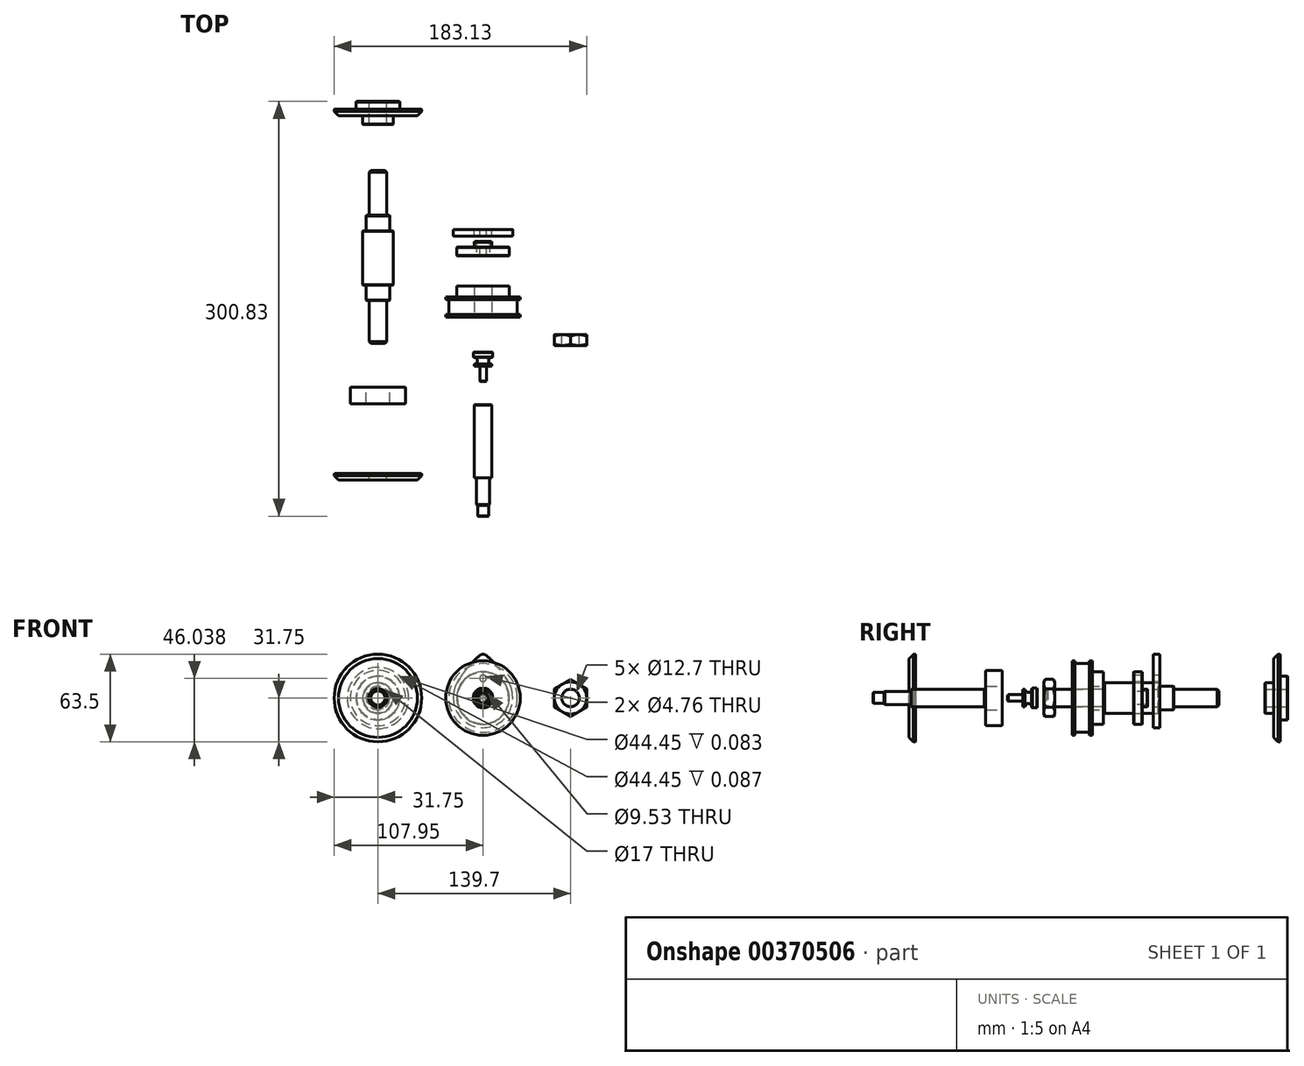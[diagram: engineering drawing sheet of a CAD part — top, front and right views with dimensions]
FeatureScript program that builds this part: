
annotation { "Feature Type Name" : "Feature", "Feature Type Description" : "" }
export const myFeature = defineFeature(function(context is Context, id is Id, definition is map)
    precondition{}
    {
        {
            var Q0;
            Q0=qCreatedBy(makeId("Right.planeOp"),FACE);
            var sketch = newSketch(context, id + "F0", { "sketchPlane" : qUnion([Q0])});
            skLineSegment(sketch, "E0", {"start": v(-34.13, 0) * mm, "end": v(-34.13, 2.38) * mm});
            skLineSegment(sketch, "E1", {"start": v(-34.13, 2.38) * mm, "end": v(-23.02, 2.38) * mm});
            skLineSegment(sketch, "E2", {"start": v(-23.02, 2.38) * mm, "end": v(-23.02, 6.35) * mm});
            skLineSegment(sketch, "E3", {"start": v(-23.02, 6.35) * mm, "end": v(-21.43, 6.35) * mm});
            skLineSegment(sketch, "E4", {"start": v(-16.67, 6.35) * mm, "end": v(-16.67, 7.14) * mm});
            skLineSegment(sketch, "E5", {"start": v(-16.67, 7.14) * mm, "end": v(-12.7, 7.14) * mm});
            skLineSegment(sketch, "E6", {"start": v(-12.7, 7.14) * mm, "end": v(-12.7, 0) * mm});
            skLineSegment(sketch, "E7", {"start": v(0, 0) * mm, "end": v(-162.62, 0) * mm, "construction": true});
            skLineSegment(sketch, "E8", {"start": v(-12.7, 0) * mm, "end": v(-34.13, 0) * mm});
            skArc(sketch, "E9", {"start": v(-21.43, 6.35) * mm, "mid": v(-19.05, 3.97) * mm, "end": v(-16.67, 6.35) * mm});
            skSolve(sketch);
        }
        {
            var Q0;
            Q0=makeQuery(id+"F0.imprint","IMPRINT",FACE,{"disambiguationData":[TD([[makeQuery(id+"F0.imprint","IMPRINT",EDGE,{"derivedFrom":sQuery(id+"F0.wireOp",EDGE,"E0")}),-1.0]])]});
            var Q1;
            Q1=sQuery(id+"F0.wireOp",EDGE,"E7");
            revolve(context, id + "F1", {"entities" : qUnion([Q0]), "axis" : qUnion([Q1]), "revolveType" : RevolveType.FULL});
        }
        {
            var Q0;
            Q0=makeQuery(id+"F1.opRevolve","SWEPT_FACE",FACE,{"disambiguationData":[OSD([sQuery(id+"F0.wireOp",EDGE,"E5")])]});
            var Q1;
            Q1=makeQuery(id+"F1.opRevolve","SWEPT_EDGE",EDGE,{"disambiguationData":[OSD([sQuery(id+"F0.wireOp",EDGE,"E0"),sQuery(id+"F0.wireOp",EDGE,"E1")])]});
            chamfer(context, id + "F2", {"entities" : qUnion([Q0, Q1]), "width" : 0.4 * mm, "tangentPropagation" : true});
        }
        {
            var Q0;
            Q0=makeQuery(id+"F1.opRevolve","SWEPT_EDGE",EDGE,{"disambiguationData":[OSD([sQuery(id+"F0.wireOp",EDGE,"E1"),sQuery(id+"F0.wireOp",EDGE,"E2")])]});
            fillet(context, id + "F3", {"entities" : qUnion([Q0]), "radius" : 0.4 * mm, "tangentPropagation" : true, "allowEdgeOverflow" : false});
        }
        {
            var Q0;
            Q0=qCreatedBy(makeId("Right.planeOp"),FACE);
            var sketch = newSketch(context, id + "F4", { "sketchPlane" : qUnion([Q0])});
            skLineSegment(sketch, "E10", {"start": v(0, 0) * mm, "end": v(30.35, 0) * mm, "construction": true});
            skLineSegment(sketch, "E11", {"start": v(12.7, 6.35) * mm, "end": v(12.7, 27) * mm});
            skLineSegment(sketch, "E12", {"start": v(12.7, 27) * mm, "end": v(14.7, 27) * mm});
            skLineSegment(sketch, "E13", {"start": v(14.7, 27) * mm, "end": v(14.7, 24.9) * mm});
            skLineSegment(sketch, "E14", {"start": v(14.7, 24.9) * mm, "end": v(25.2, 24.9) * mm});
            skLineSegment(sketch, "E15", {"start": v(25.2, 24.9) * mm, "end": v(25.2, 27) * mm});
            skLineSegment(sketch, "E16", {"start": v(25.2, 27) * mm, "end": v(27.2, 27) * mm});
            skLineSegment(sketch, "E17", {"start": v(27.2, 27) * mm, "end": v(27.2, 19) * mm});
            skLineSegment(sketch, "E18", {"start": v(27.2, 19) * mm, "end": v(35.2, 19) * mm});
            skLineSegment(sketch, "E19", {"start": v(35.2, 19) * mm, "end": v(35.2, 6.35) * mm});
            skLineSegment(sketch, "E20", {"start": v(35.2, 6.35) * mm, "end": v(12.7, 6.35) * mm});
            skSolve(sketch);
        }
        {
            var Q0;
            Q0=makeQuery(id+"F4.imprint","IMPRINT",FACE,{"disambiguationData":[TD([[makeQuery(id+"F4.imprint","IMPRINT",EDGE,{"derivedFrom":sQuery(id+"F4.wireOp",EDGE,"E11")}),-1.0]])]});
            var Q1;
            Q1=sQuery(id+"F4.wireOp",EDGE,"E10");
            revolve(context, id + "F5", {"entities" : qUnion([Q0]), "axis" : qUnion([Q1]), "revolveType" : RevolveType.FULL});
        }
        {
            var Q0;
            Q0=qCreatedBy(makeId("Right.planeOp"),FACE);
            var sketch = newSketch(context, id + "F6", { "sketchPlane" : qUnion([Q0])});
            skLineSegment(sketch, "E21", {"start": v(0, 0) * mm, "end": v(-138.04, 0) * mm, "construction": true});
            skLineSegment(sketch, "E22", {"start": v(-131.76, 0) * mm, "end": v(-131.76, 3.97) * mm});
            skLineSegment(sketch, "E23", {"start": v(-131.76, 3.97) * mm, "end": v(-123.83, 3.97) * mm});
            skLineSegment(sketch, "E24", {"start": v(-123.83, 3.97) * mm, "end": v(-123.83, 4.76) * mm});
            skLineSegment(sketch, "E25", {"start": v(-123.83, 4.76) * mm, "end": v(-103.98, 4.76) * mm});
            skLineSegment(sketch, "E26", {"start": v(-103.98, 4.76) * mm, "end": v(-103.98, 6.35) * mm});
            skLineSegment(sketch, "E27", {"start": v(-103.98, 6.35) * mm, "end": v(-50.8, 6.35) * mm});
            skLineSegment(sketch, "E28", {"start": v(-50.8, 6.35) * mm, "end": v(-50.8, 0) * mm});
            skLineSegment(sketch, "E29", {"start": v(-50.8, 0) * mm, "end": v(-131.76, 0) * mm});
            skSolve(sketch);
        }
        {
            var Q0;
            Q0=makeQuery(id+"F6.imprint","IMPRINT",FACE,{"disambiguationData":[TD([[makeQuery(id+"F6.imprint","IMPRINT",EDGE,{"derivedFrom":sQuery(id+"F6.wireOp",EDGE,"E22")}),-1.0]])]});
            var Q1;
            Q1=sQuery(id+"F6.wireOp",EDGE,"E21");
            revolve(context, id + "F7", {"entities" : qUnion([Q0]), "axis" : qUnion([Q1]), "revolveType" : RevolveType.FULL});
        }
        {
            var Q0;
            Q0=makeQuery(id+"F7.opRevolve","SWEPT_EDGE",EDGE,{"disambiguationData":[OSD([sQuery(id+"F6.wireOp",EDGE,"E27"),sQuery(id+"F6.wireOp",EDGE,"E28")])]});
            var Q1;
            Q1=makeQuery(id+"F7.opRevolve","SWEPT_EDGE",EDGE,{"disambiguationData":[OSD([sQuery(id+"F6.wireOp",EDGE,"E22"),sQuery(id+"F6.wireOp",EDGE,"E23")])]});
            chamfer(context, id + "F8", {"entities" : qUnion([Q0, Q1]), "width" : 0.4 * mm, "tangentPropagation" : true});
        }
        {
            var Q0;
            Q0=makeQuery(id+"F7.opRevolve","SWEPT_EDGE",EDGE,{"disambiguationData":[OSD([sQuery(id+"F6.wireOp",EDGE,"E24"),sQuery(id+"F6.wireOp",EDGE,"E25")])]});
            chamfer(context, id + "F9", {"entities" : qUnion([Q0]), "width" : 0.64 * mm, "tangentPropagation" : true});
        }
        {
            var Q0;
            Q0=makeQuery(id+"F7.opRevolve","SWEPT_EDGE",EDGE,{"disambiguationData":[OSD([sQuery(id+"F6.wireOp",EDGE,"E25"),sQuery(id+"F6.wireOp",EDGE,"E26")])]});
            fillet(context, id + "F10", {"entities" : qUnion([Q0]), "radius" : 0.4 * mm, "tangentPropagation" : true, "allowEdgeOverflow" : false});
        }
        {
            var Q0;
            Q0=qCreatedBy(makeId("Right.planeOp"),FACE);
            var sketch = newSketch(context, id + "F11", { "sketchPlane" : qUnion([Q0])});
            skLineSegment(sketch, "E30", {"start": v(0, 0) * mm, "end": v(68.22, 0) * mm, "construction": true});
            skLineSegment(sketch, "E31", {"start": v(67.47, 4.76) * mm, "end": v(57.15, 4.76) * mm});
            skLineSegment(sketch, "E32", {"start": v(57.15, 4.76) * mm, "end": v(57.15, 19.05) * mm});
            skLineSegment(sketch, "E33", {"start": v(57.15, 19.05) * mm, "end": v(63.5, 19.05) * mm});
            skLineSegment(sketch, "E34", {"start": v(63.5, 19.05) * mm, "end": v(63.5, 6.35) * mm});
            skLineSegment(sketch, "E35", {"start": v(63.5, 6.35) * mm, "end": v(67.47, 6.35) * mm});
            skLineSegment(sketch, "E36", {"start": v(67.47, 6.35) * mm, "end": v(67.47, 4.76) * mm});
            skSolve(sketch);
        }
        {
            var Q0;
            Q0=makeQuery(id+"F11.imprint","IMPRINT",FACE,{"disambiguationData":[TD([[makeQuery(id+"F11.imprint","IMPRINT",EDGE,{"derivedFrom":sQuery(id+"F11.wireOp",EDGE,"E31")}),-1.0]])]});
            var Q1;
            Q1=sQuery(id+"F11.wireOp",EDGE,"E30");
            revolve(context, id + "F12", {"entities" : qUnion([Q0]), "axis" : qUnion([Q1]), "revolveType" : RevolveType.FULL});
        }
        {
            var Q0;
            Q0=makeQuery(id+"F12.opRevolve","SWEPT_FACE",FACE,{"disambiguationData":[OSD([sQuery(id+"F11.wireOp",EDGE,"E36")])]});
            var Q1;
            Q1=makeQuery(id+"F12.opRevolve","SWEPT_FACE",FACE,{"disambiguationData":[OSD([sQuery(id+"F11.wireOp",EDGE,"E33")])]});
            var Q2;
            Q2=makeQuery(id+"F12.opRevolve","SWEPT_EDGE",EDGE,{"disambiguationData":[OSD([sQuery(id+"F11.wireOp",EDGE,"E31"),sQuery(id+"F11.wireOp",EDGE,"E32")])]});
            chamfer(context, id + "F13", {"entities" : qUnion([Q0, Q1, Q2]), "width" : 0.4 * mm, "tangentPropagation" : true});
        }
        {
            var Q0;
            Q0=makeQuery(id+"F12.opRevolve","SWEPT_EDGE",EDGE,{"disambiguationData":[OSD([sQuery(id+"F11.wireOp",EDGE,"E34"),sQuery(id+"F11.wireOp",EDGE,"E35")])]});
            fillet(context, id + "F14", {"entities" : qUnion([Q0]), "radius" : 0.4 * mm, "tangentPropagation" : true, "allowEdgeOverflow" : false});
        }
        {
            var Q0;
            Q0=qCreatedBy(makeId("Front.planeOp"),FACE);
            cPlane(context, id + "F15", {"entities" : qUnion([Q0]), "cplaneType" : CPlaneType.OFFSET, "offset" : 76.2 * mm, "oppositeDirection" : true, "width" : 152.4 * mm, "height" : 152.4 * mm});
        }
        {
            var Q0;
            Q0=qCreatedBy(id+"F15.planeOp",FACE);
            var sketch = newSketch(context, id + "F16", { "sketchPlane" : qUnion([Q0])});
            skCircle(sketch, "E37", {"center": v(0, 0) * mm, "radius": 6.35 * mm});
            skArc(sketch, "E38", {"start": v(-21.38, 2.39) * mm, "mid": v(-0.06, -21.51) * mm, "end": v(21.4, 2.27) * mm});
            skCircle(sketch, "E39", {"center": v(0, 14.29) * mm, "radius": 2.38 * mm});
            skArc(sketch, "E40", {"start": v(2.18, 30.95) * mm, "mid": v(0, 31.74) * mm, "end": v(-2.18, 30.95) * mm});
            skLineSegment(sketch, "E41", {"start": v(0, 0) * mm, "end": v(-43.39, -24.05) * mm, "construction": true});
            skLineSegment(sketch, "E42", {"start": v(0, 0) * mm, "end": v(43.39, -24.05) * mm, "construction": true});
            skArc(sketch, "E43", {"start": v(-2.18, 30.95) * mm, "mid": v(-11.58, 21.55) * mm, "end": v(-19.08, 10.58) * mm});
            skArc(sketch, "E44.trimOffspring", {"start": v(19.1, 10.58) * mm, "mid": v(11.59, 21.56) * mm, "end": v(2.18, 30.95) * mm});
            skLineSegment(sketch, "E45", {"start": v(0, 0) * mm, "end": v(19.1, 10.58) * mm, "construction": true});
            skArc(sketch, "E46", {"start": v(21.23, 3.8) * mm, "mid": v(20.5, 7.3) * mm, "end": v(19.1, 10.58) * mm});
            skLineSegment(sketch, "E47", {"start": v(21.4, 2.27) * mm, "end": v(21.23, 3.8) * mm});
            skLineSegment(sketch, "E48", {"start": v(0, 0) * mm, "end": v(-19.08, 10.58) * mm, "construction": true});
            skArc(sketch, "E49", {"start": v(-19.08, 10.58) * mm, "mid": v(-20.48, 7.35) * mm, "end": v(-21.21, 3.9) * mm});
            skLineSegment(sketch, "E50", {"start": v(-21.21, 3.9) * mm, "end": v(-21.38, 2.39) * mm});
            skSolve(sketch);
        }
        {
            var Q0;
            Q0=makeQuery(id+"F16.imprint","IMPRINT",FACE,{"disambiguationData":[TD([[makeQuery(id+"F16.imprint","IMPRINT",EDGE,{"derivedFrom":sQuery(id+"F16.wireOp",EDGE,"E37")}),-1.0]])]});
            extrude(context, id + "F17", {"entities" : qUnion([Q0]), "depth" : 4.76 * mm});
        }
        {
            var Q0;
            Q0=makeQuery(id+"F16.imprint","IMPRINT",FACE,{"disambiguationData":[TD([[makeQuery(id+"F16.imprint","IMPRINT",EDGE,{"derivedFrom":sQuery(id+"F16.wireOp",EDGE,"E39")}),1.0]])]});
            extrude(context, id + "F18", {"entities" : qUnion([Q0]), "operationType" : NewBodyOperationType.REMOVE, "depth" : 25.4 * mm});
        }
        {
            var Q0;
            Q0=qCreatedBy(makeId("Top.planeOp"),FACE);
            var sketch = newSketch(context, id + "F19", { "sketchPlane" : qUnion([Q0])});
            skLineSegment(sketch, "E51", {"start": v(-76.2, 204.41) * mm, "end": v(-76.2, -130.74) * mm, "construction": true});
            skLineSegment(sketch, "E52", {"start": v(-98.42, -100.8) * mm, "end": v(-107.95, -100.8) * mm});
            skLineSegment(sketch, "E53", {"start": v(-107.95, -100.8) * mm, "end": v(-107.95, -102.39) * mm});
            skLineSegment(sketch, "E54", {"start": v(-107.95, -102.39) * mm, "end": v(-104.77, -105.56) * mm});
            skLineSegment(sketch, "E55", {"start": v(-104.77, -105.56) * mm, "end": v(-82.55, -105.56) * mm});
            skLineSegment(sketch, "E56", {"start": v(-82.55, -105.56) * mm, "end": v(-82.55, -101.6) * mm});
            skLineSegment(sketch, "E57", {"start": v(-82.55, -101.6) * mm, "end": v(-98.42, -101.6) * mm});
            skLineSegment(sketch, "E58", {"start": v(-98.42, -101.6) * mm, "end": v(-98.42, -100.8) * mm});
            skLineSegment(sketch, "E59.bottom", {"start": v(-95.6, -50.1) * mm, "end": v(-85.3, -50.1) * mm});
            skLineSegment(sketch, "E59.top", {"start": v(-95.6, -38.1) * mm, "end": v(-85.3, -38.1) * mm});
            skLineSegment(sketch, "E59.left", {"start": v(-96.2, -49.5) * mm, "end": v(-96.2, -38.7) * mm});
            skLineSegment(sketch, "E59.right", {"start": v(-84.7, -49.5) * mm, "end": v(-84.7, -38.7) * mm});
            skPoint(sketch, "E60.visualSharp", {"position": v(-96.2, -50.1) * mm});
            skArc(sketch, "E60.filletArc", {"start": v(-96.2, -49.5) * mm, "mid": v(-96.02, -49.92) * mm, "end": v(-95.6, -50.1) * mm});
            skPoint(sketch, "E61.visualSharp", {"position": v(-96.2, -38.1) * mm});
            skArc(sketch, "E61.filletArc", {"start": v(-95.6, -38.1) * mm, "mid": v(-96.02, -38.28) * mm, "end": v(-96.2, -38.7) * mm});
            skPoint(sketch, "E62.visualSharp", {"position": v(-84.7, -38.1) * mm});
            skArc(sketch, "E62.filletArc", {"start": v(-84.7, -38.7) * mm, "mid": v(-84.88, -38.28) * mm, "end": v(-85.3, -38.1) * mm});
            skPoint(sketch, "E63.visualSharp", {"position": v(-84.7, -50.1) * mm});
            skArc(sketch, "E63.filletArc", {"start": v(-85.3, -50.1) * mm, "mid": v(-84.88, -49.92) * mm, "end": v(-84.7, -49.5) * mm});
            skLineSegment(sketch, "E64", {"start": v(-76.2, -6.35) * mm, "end": v(-82.55, -6.35) * mm});
            skLineSegment(sketch, "E65", {"start": v(-82.55, -6.35) * mm, "end": v(-82.55, 24.6) * mm});
            skLineSegment(sketch, "E66", {"start": v(-82.55, 24.6) * mm, "end": v(-84.7, 24.6) * mm});
            skLineSegment(sketch, "E67", {"start": v(-84.7, 24.6) * mm, "end": v(-84.7, 35.81) * mm});
            skLineSegment(sketch, "E68", {"start": v(-84.7, 35.81) * mm, "end": v(-87.31, 35.81) * mm});
            skLineSegment(sketch, "E69", {"start": v(-87.31, 35.81) * mm, "end": v(-87.31, 75.31) * mm});
            skLineSegment(sketch, "E70", {"start": v(-87.31, 75.31) * mm, "end": v(-84.7, 75.31) * mm});
            skLineSegment(sketch, "E71", {"start": v(-84.7, 75.31) * mm, "end": v(-84.7, 86.5) * mm});
            skLineSegment(sketch, "E72", {"start": v(-84.7, 86.5) * mm, "end": v(-82.55, 86.5) * mm});
            skLineSegment(sketch, "E73", {"start": v(-82.55, 86.5) * mm, "end": v(-82.55, 119.05) * mm});
            skLineSegment(sketch, "E74", {"start": v(-82.55, 119.05) * mm, "end": v(-76.2, 119.05) * mm});
            skLineSegment(sketch, "E75", {"start": v(-76.2, 119.05) * mm, "end": v(-76.2, -6.35) * mm});
            skLineSegment(sketch, "E76", {"start": v(-82.55, 152.4) * mm, "end": v(-87.31, 152.4) * mm});
            skLineSegment(sketch, "E77", {"start": v(-87.31, 152.4) * mm, "end": v(-87.31, 158.75) * mm});
            skLineSegment(sketch, "E78", {"start": v(-87.31, 158.75) * mm, "end": v(-104.78, 158.75) * mm});
            skLineSegment(sketch, "E79", {"start": v(-104.78, 158.75) * mm, "end": v(-107.95, 161.93) * mm});
            skLineSegment(sketch, "E80", {"start": v(-107.95, 161.93) * mm, "end": v(-107.95, 163.51) * mm});
            skLineSegment(sketch, "E81", {"start": v(-107.95, 163.51) * mm, "end": v(-98.43, 163.51) * mm});
            skLineSegment(sketch, "E82", {"start": v(-98.43, 163.51) * mm, "end": v(-98.43, 162.72) * mm});
            skLineSegment(sketch, "E83", {"start": v(-98.43, 162.72) * mm, "end": v(-92.08, 162.72) * mm});
            skLineSegment(sketch, "E84", {"start": v(-92.08, 162.72) * mm, "end": v(-92.08, 169.07) * mm});
            skLineSegment(sketch, "E85", {"start": v(-92.08, 169.07) * mm, "end": v(-82.55, 169.07) * mm});
            skLineSegment(sketch, "E86", {"start": v(-82.55, 169.07) * mm, "end": v(-82.55, 152.4) * mm});
            skSolve(sketch);
        }
        {
            var Q0;
            Q0=makeQuery(id+"F19.imprint","IMPRINT",FACE,{"disambiguationData":[TD([[makeQuery(id+"F19.imprint","IMPRINT",EDGE,{"derivedFrom":sQuery(id+"F19.wireOp",EDGE,"E52")}),1.0]])]});
            var Q1;
            Q1=makeQuery(id+"F19.imprint","IMPRINT",FACE,{"disambiguationData":[TD([[makeQuery(id+"F19.imprint","IMPRINT",EDGE,{"derivedFrom":sQuery(id+"F19.wireOp",EDGE,"E59.bottom")}),1.0]])]});
            var Q2;
            Q2=makeQuery(id+"F19.imprint","IMPRINT",FACE,{"disambiguationData":[TD([[makeQuery(id+"F19.imprint","IMPRINT",EDGE,{"derivedFrom":sQuery(id+"F19.wireOp",EDGE,"E64")}),-1.0]])]});
            var Q3;
            Q3=makeQuery(id+"F19.imprint","IMPRINT",FACE,{"disambiguationData":[TD([[makeQuery(id+"F19.imprint","IMPRINT",EDGE,{"derivedFrom":sQuery(id+"F19.wireOp",EDGE,"E76")}),-1.0]])]});
            var Q4;
            Q4=sQuery(id+"F19.wireOp",EDGE,"E51");
            revolve(context, id + "F20", {"entities" : qUnion([Q0, Q1, Q2, Q3]), "axis" : qUnion([Q4]), "revolveType" : RevolveType.FULL});
        }
        {
            var Q0;
            Q0=makeQuery(id+"F20.opRevolve","SWEPT_EDGE",EDGE,{"disambiguationData":[OSD([sQuery(id+"F19.wireOp",EDGE,"E64"),sQuery(id+"F19.wireOp",EDGE,"E65")])]});
            var Q1;
            Q1=makeQuery(id+"F20.opRevolve","SWEPT_EDGE",EDGE,{"disambiguationData":[OSD([sQuery(id+"F19.wireOp",EDGE,"E73"),sQuery(id+"F19.wireOp",EDGE,"E74")])]});
            chamfer(context, id + "F21", {"entities" : qUnion([Q0, Q1]), "width" : 1.2 * mm, "tangentPropagation" : true});
        }
        {
            var Q0;
            Q0=makeQuery(id+"F20.opRevolve","SWEPT_FACE",FACE,{"disambiguationData":[OSD([sQuery(id+"F19.wireOp",EDGE,"E56")])]});
            var Q1;
            Q1=makeQuery(id+"F20.opRevolve","SWEPT_FACE",FACE,{"disambiguationData":[OSD([sQuery(id+"F19.wireOp",EDGE,"E86")])]});
            var Q2;
            Q2=makeQuery(id+"F20.opRevolve","SWEPT_EDGE",EDGE,{"disambiguationData":[OSD([sQuery(id+"F19.wireOp",EDGE,"E76"),sQuery(id+"F19.wireOp",EDGE,"E77")])]});
            var Q3;
            Q3=makeQuery(id+"F20.opRevolve","SWEPT_EDGE",EDGE,{"disambiguationData":[OSD([sQuery(id+"F19.wireOp",EDGE,"E66"),sQuery(id+"F19.wireOp",EDGE,"E67")])]});
            var Q4;
            Q4=makeQuery(id+"F20.opRevolve","SWEPT_EDGE",EDGE,{"disambiguationData":[OSD([sQuery(id+"F19.wireOp",EDGE,"E68"),sQuery(id+"F19.wireOp",EDGE,"E69")])]});
            var Q5;
            Q5=makeQuery(id+"F20.opRevolve","SWEPT_EDGE",EDGE,{"disambiguationData":[OSD([sQuery(id+"F19.wireOp",EDGE,"E69"),sQuery(id+"F19.wireOp",EDGE,"E70")])]});
            var Q6;
            Q6=makeQuery(id+"F20.opRevolve","SWEPT_EDGE",EDGE,{"disambiguationData":[OSD([sQuery(id+"F19.wireOp",EDGE,"E71"),sQuery(id+"F19.wireOp",EDGE,"E72")])]});
            var Q7;
            Q7=makeQuery(id+"F20.opRevolve","SWEPT_EDGE",EDGE,{"disambiguationData":[OSD([sQuery(id+"F19.wireOp",EDGE,"E52"),sQuery(id+"F19.wireOp",EDGE,"E53")])]});
            var Q8;
            Q8=makeQuery(id+"F20.opRevolve","SWEPT_EDGE",EDGE,{"disambiguationData":[OSD([sQuery(id+"F19.wireOp",EDGE,"E84"),sQuery(id+"F19.wireOp",EDGE,"E85")])]});
            var Q9;
            Q9=makeQuery(id+"F20.opRevolve","SWEPT_EDGE",EDGE,{"disambiguationData":[OSD([sQuery(id+"F19.wireOp",EDGE,"E80"),sQuery(id+"F19.wireOp",EDGE,"E81")])]});
            chamfer(context, id + "F22", {"entities" : qUnion([Q0, Q1, Q2, Q3, Q4, Q5, Q6, Q7, Q8, Q9]), "width" : 0.4 * mm, "tangentPropagation" : true});
        }
        {
            var Q0;
            Q0=makeQuery(id+"F20.opRevolve","SWEPT_EDGE",EDGE,{"disambiguationData":[OSD([sQuery(id+"F19.wireOp",EDGE,"E82"),sQuery(id+"F19.wireOp",EDGE,"E83")])]});
            var Q1;
            Q1=makeQuery(id+"F20.opRevolve","SWEPT_EDGE",EDGE,{"disambiguationData":[OSD([sQuery(id+"F19.wireOp",EDGE,"E57"),sQuery(id+"F19.wireOp",EDGE,"E58")])]});
            var Q2;
            Q2=makeQuery(id+"F20.opRevolve","SWEPT_EDGE",EDGE,{"disambiguationData":[OSD([sQuery(id+"F19.wireOp",EDGE,"E72"),sQuery(id+"F19.wireOp",EDGE,"E73")])]});
            var Q3;
            Q3=makeQuery(id+"F20.opRevolve","SWEPT_EDGE",EDGE,{"disambiguationData":[OSD([sQuery(id+"F19.wireOp",EDGE,"E65"),sQuery(id+"F19.wireOp",EDGE,"E66")])]});
            fillet(context, id + "F23", {"entities" : qUnion([Q0, Q1, Q2, Q3]), "radius" : 0.71 * mm, "tangentPropagation" : true, "allowEdgeOverflow" : false});
        }
        {
            var Q0;
            Q0=makeQuery(id+"F20.opRevolve","SWEPT_EDGE",EDGE,{"disambiguationData":[OSD([sQuery(id+"F19.wireOp",EDGE,"E67"),sQuery(id+"F19.wireOp",EDGE,"E68")])]});
            var Q1;
            Q1=makeQuery(id+"F20.opRevolve","SWEPT_EDGE",EDGE,{"disambiguationData":[OSD([sQuery(id+"F19.wireOp",EDGE,"E70"),sQuery(id+"F19.wireOp",EDGE,"E71")])]});
            var Q2;
            Q2=makeQuery(id+"F5.opRevolve","SWEPT_EDGE",EDGE,{"disambiguationData":[OSD([sQuery(id+"F4.wireOp",EDGE,"E17"),sQuery(id+"F4.wireOp",EDGE,"E18")])]});
            fillet(context, id + "F24", {"entities" : qUnion([Q0, Q1, Q2]), "radius" : 0.38 * mm, "tangentPropagation" : true, "allowEdgeOverflow" : false});
        }
        {
            var Q0;
            Q0=qCreatedBy(makeId("Front.planeOp"),FACE);
            var sketch = newSketch(context, id + "F25", { "sketchPlane" : qUnion([Q0])});
            skCircle(sketch, "E87.cCircle", {"center": v(63.5, 0) * mm, "radius": 11.68 * mm, "construction": true});
            skLineSegment(sketch, "E87.0", {"start": v(51.82, -6.75) * mm, "end": v(51.82, 6.75) * mm});
            skLineSegment(sketch, "E87.1", {"start": v(51.82, 6.75) * mm, "end": v(63.5, 13.5) * mm});
            skLineSegment(sketch, "E87.2", {"start": v(63.5, 13.5) * mm, "end": v(75.18, 6.75) * mm});
            skLineSegment(sketch, "E87.3", {"start": v(75.18, 6.75) * mm, "end": v(75.18, -6.75) * mm});
            skLineSegment(sketch, "E87.4", {"start": v(75.18, -6.75) * mm, "end": v(63.5, -13.5) * mm});
            skLineSegment(sketch, "E87.5", {"start": v(63.5, -13.5) * mm, "end": v(51.82, -6.75) * mm});
            skPoint(sketch, "E87.0.midPoint", {"position": v(51.82, 0) * mm});
            skCircle(sketch, "E88", {"center": v(63.5, 0) * mm, "radius": 6.35 * mm});
            skSolve(sketch);
        }
        {
            var Q0;
            Q0=makeQuery(id+"F25.imprint","IMPRINT",FACE,{"disambiguationData":[TD([[makeQuery(id+"F25.imprint","IMPRINT",EDGE,{"derivedFrom":sQuery(id+"F25.wireOp",EDGE,"E87.0")}),-1.0]])]});
            extrude(context, id + "F26", {"entities" : qUnion([Q0]), "depth" : 7.94 * mm});
        }
        {
            var Q0;
            Q0=qCreatedBy(makeId("Top.planeOp"),FACE);
            var sketch = newSketch(context, id + "F27", { "sketchPlane" : qUnion([Q0])});
            skLineSegment(sketch, "E89", {"start": v(51.82, 0) * mm, "end": v(49.28, -1.47) * mm});
            skLineSegment(sketch, "E90", {"start": v(49.28, -1.47) * mm, "end": v(49.28, 0) * mm});
            skLineSegment(sketch, "E91", {"start": v(49.28, 0) * mm, "end": v(51.82, 0) * mm});
            skLineSegment(sketch, "E92", {"start": v(51.82, -7.94) * mm, "end": v(49.28, -7.94) * mm});
            skLineSegment(sketch, "E93", {"start": v(49.28, -7.94) * mm, "end": v(49.28, -6.47) * mm});
            skLineSegment(sketch, "E94", {"start": v(49.28, -6.47) * mm, "end": v(51.82, -7.94) * mm});
            skSolve(sketch);
        }
        {
            var Q0;
            Q0=makeQuery(id+"F27.imprint","IMPRINT",FACE,{"disambiguationData":[TD([[makeQuery(id+"F27.imprint","IMPRINT",EDGE,{"derivedFrom":sQuery(id+"F27.wireOp",EDGE,"E89")}),-1.0]])]});
            var Q1;
            Q1=makeQuery(id+"F27.imprint","IMPRINT",FACE,{"disambiguationData":[TD([[makeQuery(id+"F27.imprint","IMPRINT",EDGE,{"derivedFrom":sQuery(id+"F27.wireOp",EDGE,"E92")}),-1.0]])]});
            var Q2;
            Q2=makeQuery(id+"F26.opExtrude","CAP_EDGE",EDGE,{"disambiguationData":[OSD([sQuery(id+"F25.wireOp",EDGE,"E88")])],"isStart":false});
            revolve(context, id + "F28", {"operationType" : NewBodyOperationType.REMOVE, "entities" : qUnion([Q0, Q1]), "axis" : qUnion([Q2]), "revolveType" : RevolveType.FULL, "oppositeDirection" : true});
        }
    });
